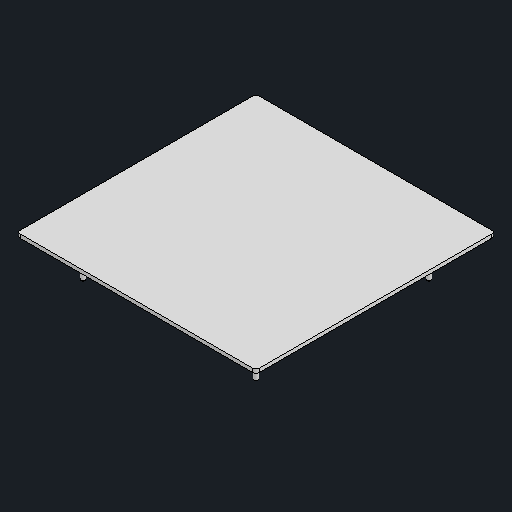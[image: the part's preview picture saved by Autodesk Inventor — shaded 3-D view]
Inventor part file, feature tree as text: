
AUTODESK INVENTOR PART (.ipt)
format: ipt  version: 2024.2 (Build 282272000, 272)  size: 2,298,880 bytes
history: native  units: mm
features: other x10, mirror x6, chamfer x1, sweep x1
ambient origin geometry x8: Origin, YZ Plane, XZ Plane, XY Plane, X Axis, Y Axis, Z Axis, Center Point
bodies: Body1 (feature_tree), Body2 (feature_tree), Body3 (feature_tree), Body4 (feature_tree), Body5 (feature_tree), Body6 (feature_tree), Body7 (feature_tree), Body8 (feature_tree), Body9 (feature_tree)
feature tree (18):
  other  "솔리드1"
  other  "솔리드2"
  other  "솔리드3"
  other  "솔리드4"
  other  "솔리드5"
  other  "솔리드6"
  other  "솔리드7"
  other  "솔리드8"
  other  "솔리드9"
  chamfer  "Chamfer1"  [1 undecoded]
  other  "Boss-Extrude3"
  sweep  "Sweep1"
  mirror  "Mirror1[1]"
  mirror  "Mirror2[1]"
  mirror  "Mirror2[2]"
  mirror  "Mirror1[2]"
  mirror  "Mirror2[3]"
  mirror  "Mirror2[4]"
note: 1 required parameter value undecoded (feature->parameter linkage not recoverable at this tier; creation-order binding heuristic only, values carry confidence <= 0.55)
